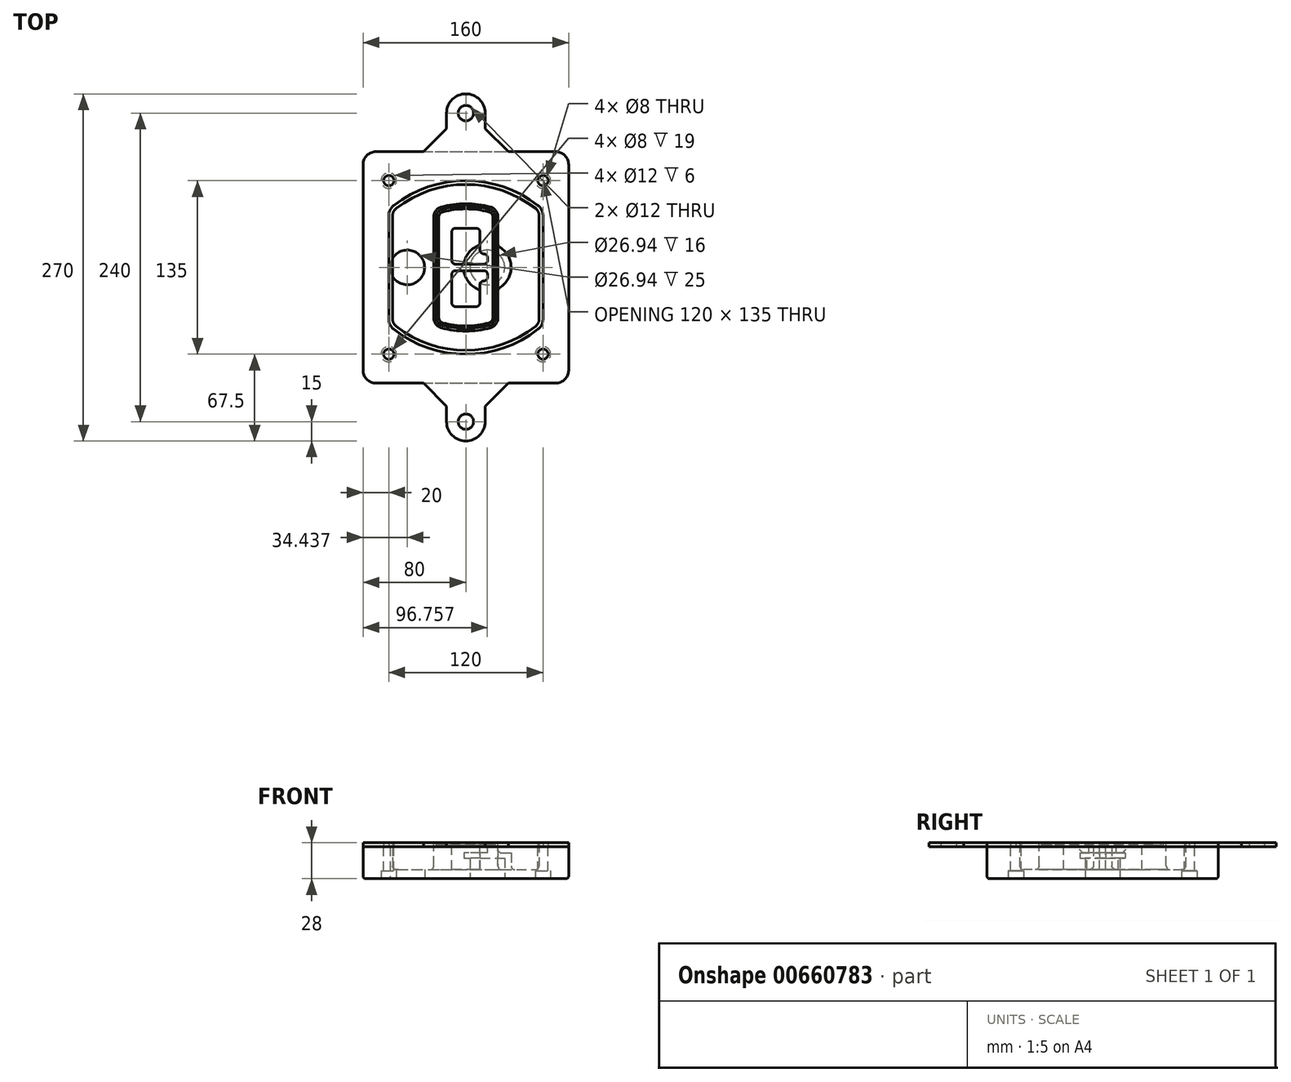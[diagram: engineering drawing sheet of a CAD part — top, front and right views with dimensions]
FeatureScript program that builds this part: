
annotation { "Feature Type Name" : "Feature", "Feature Type Description" : "" }
export const myFeature = defineFeature(function(context is Context, id is Id, definition is map)
    precondition{}
    {
        {
            var Q0;
            Q0=qCreatedBy(makeId("Top.planeOp"),FACE);
            var sketch = newSketch(context, id + "F0", { "sketchPlane" : qUnion([Q0])});
            skPoint(sketch, "E0.rect.middle", {"position": v(0, 0) * mm});
            skLineSegment(sketch, "E1.bottom", {"start": v(-70, -90) * mm, "end": v(70, -90) * mm});
            skLineSegment(sketch, "E1.top", {"start": v(-70, 90) * mm, "end": v(70, 90) * mm});
            skLineSegment(sketch, "E1.left", {"start": v(-80, -80) * mm, "end": v(-80, 80) * mm});
            skLineSegment(sketch, "E1.right", {"start": v(80, -80) * mm, "end": v(80, 80) * mm});
            skLineSegment(sketch, "E2", {"start": v(-80, 90) * mm, "end": v(80, -90) * mm, "construction": true});
            skLineSegment(sketch, "E3", {"start": v(80, 90) * mm, "end": v(-80, -90) * mm, "construction": true});
            skCircle(sketch, "E4", {"center": v(-60, 67.5) * mm, "radius": 4 * mm});
            skCircle(sketch, "E5", {"center": v(60, 67.5) * mm, "radius": 4 * mm});
            skCircle(sketch, "E6", {"center": v(60, -67.5) * mm, "radius": 4 * mm});
            skCircle(sketch, "E7", {"center": v(-60, -67.5) * mm, "radius": 4 * mm});
            skLineSegment(sketch, "E8", {"start": v(-60, 67.5) * mm, "end": v(60, 67.5) * mm, "construction": true});
            skLineSegment(sketch, "E9", {"start": v(60, 67.5) * mm, "end": v(60, -67.5) * mm, "construction": true});
            skLineSegment(sketch, "E10", {"start": v(60, -67.5) * mm, "end": v(-60, -67.5) * mm, "construction": true});
            skLineSegment(sketch, "E11", {"start": v(-60, -67.5) * mm, "end": v(-60, 67.5) * mm, "construction": true});
            skLineSegment(sketch, "E12", {"start": v(-60, 40.3) * mm, "end": v(-60, -40.3) * mm});
            skLineSegment(sketch, "E13", {"start": v(60, 40.3) * mm, "end": v(60, -40.3) * mm});
            skArc(sketch, "E14", {"start": v(56.15, 48.18) * mm, "mid": v(0, 67.5) * mm, "end": v(-56.15, 48.18) * mm});
            skArc(sketch, "E15", {"start": v(-56.15, -48.18) * mm, "mid": v(0, -67.5) * mm, "end": v(56.15, -48.18) * mm});
            skLineSegment(sketch, "E16", {"start": v(-60, 0) * mm, "end": v(60, 0) * mm, "construction": true});
            skPoint(sketch, "E17.visualSharp", {"position": v(-60, -45) * mm});
            skArc(sketch, "E17.filletArc", {"start": v(-60, -40.3) * mm, "mid": v(-58.99, -44.68) * mm, "end": v(-56.15, -48.18) * mm});
            skPoint(sketch, "E18.visualSharp", {"position": v(-60, 45) * mm});
            skArc(sketch, "E18.filletArc", {"start": v(-56.15, 48.18) * mm, "mid": v(-58.99, 44.68) * mm, "end": v(-60, 40.3) * mm});
            skPoint(sketch, "E19.visualSharp", {"position": v(60, 45) * mm});
            skArc(sketch, "E19.filletArc", {"start": v(60, 40.3) * mm, "mid": v(58.99, 44.68) * mm, "end": v(56.15, 48.18) * mm});
            skPoint(sketch, "E20.visualSharp", {"position": v(60, -45) * mm});
            skArc(sketch, "E20.filletArc", {"start": v(56.15, -48.18) * mm, "mid": v(58.99, -44.68) * mm, "end": v(60, -40.3) * mm});
            skPoint(sketch, "E21.visualSharp", {"position": v(-80, 90) * mm});
            skArc(sketch, "E21.filletArc", {"start": v(-70, 90) * mm, "mid": v(-77.07, 87.07) * mm, "end": v(-80, 80) * mm});
            skPoint(sketch, "E22.visualSharp", {"position": v(80, 90) * mm});
            skArc(sketch, "E22.filletArc", {"start": v(80, 80) * mm, "mid": v(77.07, 87.07) * mm, "end": v(70, 90) * mm});
            skPoint(sketch, "E23.visualSharp", {"position": v(80, -90) * mm});
            skArc(sketch, "E23.filletArc", {"start": v(70, -90) * mm, "mid": v(77.07, -87.07) * mm, "end": v(80, -80) * mm});
            skPoint(sketch, "E24.visualSharp", {"position": v(-80, -90) * mm});
            skArc(sketch, "E24.filletArc", {"start": v(-80, -80) * mm, "mid": v(-77.07, -87.07) * mm, "end": v(-70, -90) * mm});
            skArc(sketch, "E25.0", {"start": v(57, 40.3) * mm, "mid": v(56.3, 43.36) * mm, "end": v(54.3, 45.81) * mm});
            skLineSegment(sketch, "E25.1", {"start": v(57, 40.3) * mm, "end": v(57, -40.3) * mm});
            skArc(sketch, "E25.2", {"start": v(54.3, -45.81) * mm, "mid": v(56.3, -43.36) * mm, "end": v(57, -40.3) * mm});
            skArc(sketch, "E25.3", {"start": v(-54.3, -45.81) * mm, "mid": v(0, -64.5) * mm, "end": v(54.3, -45.81) * mm});
            skArc(sketch, "E25.4", {"start": v(-57, -40.3) * mm, "mid": v(-56.3, -43.36) * mm, "end": v(-54.3, -45.81) * mm});
            skArc(sketch, "E25.5", {"start": v(54.3, 45.81) * mm, "mid": v(0, 64.5) * mm, "end": v(-54.3, 45.81) * mm});
            skLineSegment(sketch, "E25.6", {"start": v(-57, 40.3) * mm, "end": v(-57, -40.3) * mm});
            skArc(sketch, "E25.7", {"start": v(-54.3, 45.81) * mm, "mid": v(-56.3, 43.36) * mm, "end": v(-57, 40.3) * mm});
            skArc(sketch, "E26.0", {"start": v(-58.62, 51.33) * mm, "mid": v(-62.58, 46.43) * mm, "end": v(-64, 40.3) * mm});
            skArc(sketch, "E26.1", {"start": v(58.62, 51.33) * mm, "mid": v(0, 71.5) * mm, "end": v(-58.62, 51.33) * mm});
            skArc(sketch, "E26.2", {"start": v(64, 40.3) * mm, "mid": v(62.58, 46.43) * mm, "end": v(58.62, 51.33) * mm});
            skLineSegment(sketch, "E26.3", {"start": v(64, 40.3) * mm, "end": v(64, -40.3) * mm});
            skArc(sketch, "E26.4", {"start": v(58.62, -51.33) * mm, "mid": v(62.58, -46.43) * mm, "end": v(64, -40.3) * mm});
            skLineSegment(sketch, "E26.5", {"start": v(-64, 40.3) * mm, "end": v(-64, -40.3) * mm});
            skArc(sketch, "E26.6", {"start": v(-58.62, -51.33) * mm, "mid": v(0, -71.5) * mm, "end": v(58.62, -51.33) * mm});
            skArc(sketch, "E26.7", {"start": v(-64, -40.3) * mm, "mid": v(-62.58, -46.43) * mm, "end": v(-58.62, -51.33) * mm});
            skSolve(sketch);
        }
        {
            var Q0;
            Q0=makeQuery(id+"F0.imprint","IMPRINT",FACE,{"disambiguationData":[TD([[makeQuery(id+"F0.imprint","IMPRINT",EDGE,{"derivedFrom":sQuery(id+"F0.wireOp",EDGE,"E1.bottom")}),1.0]])]});
            var Q1;
            Q1=makeQuery(id+"F0.imprint","IMPRINT",FACE,{"disambiguationData":[TD([[makeQuery(id+"F0.imprint","IMPRINT",EDGE,{"derivedFrom":sQuery(id+"F0.wireOp",EDGE,"E12")}),1.0]])]});
            var Q2;
            Q2=makeQuery(id+"F0.imprint","IMPRINT",FACE,{"disambiguationData":[TD([[makeQuery(id+"F0.imprint","IMPRINT",EDGE,{"derivedFrom":sQuery(id+"F0.wireOp",EDGE,"E25.0")}),1.0]])]});
            var Q3;
            Q3=makeQuery(id+"F0.imprint","IMPRINT",FACE,{"disambiguationData":[TD([[makeQuery(id+"F0.imprint","IMPRINT",EDGE,{"derivedFrom":sQuery(id+"F0.wireOp",EDGE,"E12")}),-1.0]])]});
            extrude(context, id + "F1", {"entities" : qUnion([Q0, Q1, Q2, Q3]), "oppositeDirection" : true, "depth" : 25 * mm});
        }
        {
            var Q0;
            Q0=makeQuery(id+"F0.imprint","IMPRINT",FACE,{"disambiguationData":[TD([[makeQuery(id+"F0.imprint","IMPRINT",EDGE,{"derivedFrom":sQuery(id+"F0.wireOp",EDGE,"E12")}),1.0]])]});
            extrude(context, id + "F2", {"entities" : qUnion([Q0]), "operationType" : NewBodyOperationType.ADD, "depth" : 3 * mm});
        }
        {
            var Q0;
            Q0=makeQuery(id+"F0.imprint","IMPRINT",FACE,{"disambiguationData":[TD([[makeQuery(id+"F0.imprint","IMPRINT",EDGE,{"derivedFrom":sQuery(id+"F0.wireOp",EDGE,"E25.0")}),1.0]])]});
            extrude(context, id + "F3", {"entities" : qUnion([Q0]), "operationType" : NewBodyOperationType.REMOVE, "oppositeDirection" : true, "depth" : 18 * mm});
        }
        {
            var Q0;
            Q0=makeQuery(id+"F2.opExtrude","CAP_FACE",FACE,{"disambiguationData":[OSD([sQuery(id+"F0.wireOp",EDGE,"E12"),sQuery(id+"F0.wireOp",EDGE,"E13"),sQuery(id+"F0.wireOp",EDGE,"E14"),sQuery(id+"F0.wireOp",EDGE,"E15"),sQuery(id+"F0.wireOp",EDGE,"E17.filletArc"),sQuery(id+"F0.wireOp",EDGE,"E18.filletArc"),sQuery(id+"F0.wireOp",EDGE,"E19.filletArc"),sQuery(id+"F0.wireOp",EDGE,"E20.filletArc"),sQuery(id+"F0.wireOp",EDGE,"E25.0"),sQuery(id+"F0.wireOp",EDGE,"E25.1"),sQuery(id+"F0.wireOp",EDGE,"E25.2"),sQuery(id+"F0.wireOp",EDGE,"E25.3"),sQuery(id+"F0.wireOp",EDGE,"E25.4"),sQuery(id+"F0.wireOp",EDGE,"E25.5"),sQuery(id+"F0.wireOp",EDGE,"E25.6"),sQuery(id+"F0.wireOp",EDGE,"E25.7")])],"isStart":false});
            var sketch = newSketch(context, id + "F4", { "sketchPlane" : qUnion([Q0])});
            skArc(sketch, "E27.0", {"start": v(-19.08, -46.97) * mm, "mid": v(0, -49.5) * mm, "end": v(19.08, -46.97) * mm});
            skArc(sketch, "E28.0", {"start": v(19.08, 46.97) * mm, "mid": v(0, 49.5) * mm, "end": v(-19.08, 46.97) * mm});
            skLineSegment(sketch, "E29", {"start": v(-25, 39.25) * mm, "end": v(-25, -39.25) * mm});
            skLineSegment(sketch, "E30", {"start": v(25, 39.25) * mm, "end": v(25, -39.25) * mm});
            skLineSegment(sketch, "E31", {"start": v(-25, 45.1) * mm, "end": v(25, 45.1) * mm, "construction": true});
            skLineSegment(sketch, "E32", {"start": v(-25, -45.1) * mm, "end": v(25, -45.1) * mm, "construction": true});
            skPoint(sketch, "E33.visualSharp", {"position": v(-25, 45.1) * mm});
            skArc(sketch, "E33.filletArc", {"start": v(-19.08, 46.97) * mm, "mid": v(-23.35, 44.11) * mm, "end": v(-25, 39.25) * mm});
            skPoint(sketch, "E34.visualSharp", {"position": v(25, 45.1) * mm});
            skArc(sketch, "E34.filletArc", {"start": v(25, 39.25) * mm, "mid": v(23.35, 44.11) * mm, "end": v(19.08, 46.97) * mm});
            skPoint(sketch, "E35.visualSharp", {"position": v(25, -45.1) * mm});
            skArc(sketch, "E35.filletArc", {"start": v(19.08, -46.97) * mm, "mid": v(23.35, -44.11) * mm, "end": v(25, -39.25) * mm});
            skPoint(sketch, "E36.visualSharp", {"position": v(-25, -45.1) * mm});
            skArc(sketch, "E36.filletArc", {"start": v(-25, -39.25) * mm, "mid": v(-23.35, -44.11) * mm, "end": v(-19.08, -46.97) * mm});
            skArc(sketch, "E37.0", {"start": v(54.3, 45.81) * mm, "mid": v(0, 64.5) * mm, "end": v(-54.3, 45.81) * mm});
            skArc(sketch, "E37.1", {"start": v(-54.3, 45.81) * mm, "mid": v(-56.3, 43.36) * mm, "end": v(-57, 40.3) * mm});
            skLineSegment(sketch, "E37.2", {"start": v(-57, 40.3) * mm, "end": v(-57, -40.3) * mm});
            skArc(sketch, "E37.3", {"start": v(-57, -40.3) * mm, "mid": v(-56.3, -43.36) * mm, "end": v(-54.3, -45.81) * mm});
            skArc(sketch, "E37.4", {"start": v(-54.3, -45.81) * mm, "mid": v(0, -64.5) * mm, "end": v(54.3, -45.81) * mm});
            skArc(sketch, "E37.5", {"start": v(54.3, -45.81) * mm, "mid": v(56.3, -43.36) * mm, "end": v(57, -40.3) * mm});
            skLineSegment(sketch, "E37.6", {"start": v(57, 40.3) * mm, "end": v(57, -40.3) * mm});
            skArc(sketch, "E37.7", {"start": v(57, 40.3) * mm, "mid": v(56.3, 43.36) * mm, "end": v(54.3, 45.81) * mm});
            skLineSegment(sketch, "E38.0", {"start": v(23, 39.25) * mm, "end": v(23, -39.25) * mm});
            skArc(sketch, "E38.1", {"start": v(18.56, -45.04) * mm, "mid": v(21.76, -42.9) * mm, "end": v(23, -39.25) * mm});
            skArc(sketch, "E38.2", {"start": v(-18.56, -45.04) * mm, "mid": v(0, -47.5) * mm, "end": v(18.56, -45.04) * mm});
            skArc(sketch, "E38.3", {"start": v(-23, -39.25) * mm, "mid": v(-21.76, -42.9) * mm, "end": v(-18.56, -45.04) * mm});
            skLineSegment(sketch, "E38.4", {"start": v(-23, 39.25) * mm, "end": v(-23, -39.25) * mm});
            skArc(sketch, "E38.5", {"start": v(23, 39.25) * mm, "mid": v(21.76, 42.9) * mm, "end": v(18.56, 45.04) * mm});
            skArc(sketch, "E38.6", {"start": v(-18.56, 45.04) * mm, "mid": v(-21.76, 42.9) * mm, "end": v(-23, 39.25) * mm});
            skArc(sketch, "E38.7", {"start": v(18.56, 45.04) * mm, "mid": v(0, 47.5) * mm, "end": v(-18.56, 45.04) * mm});
            skArc(sketch, "E39.0", {"start": v(21, 39.25) * mm, "mid": v(20.18, 41.68) * mm, "end": v(18.04, 43.1) * mm});
            skLineSegment(sketch, "E39.1", {"start": v(21, 39.25) * mm, "end": v(21, -39.25) * mm});
            skArc(sketch, "E39.2", {"start": v(18.04, -43.1) * mm, "mid": v(20.18, -41.68) * mm, "end": v(21, -39.25) * mm});
            skArc(sketch, "E39.3", {"start": v(-18.04, -43.1) * mm, "mid": v(0, -45.5) * mm, "end": v(18.04, -43.1) * mm});
            skArc(sketch, "E39.4", {"start": v(-21, -39.25) * mm, "mid": v(-20.18, -41.68) * mm, "end": v(-18.04, -43.1) * mm});
            skArc(sketch, "E39.5", {"start": v(18.04, 43.1) * mm, "mid": v(0, 45.5) * mm, "end": v(-18.04, 43.1) * mm});
            skLineSegment(sketch, "E39.6", {"start": v(-21, 39.25) * mm, "end": v(-21, -39.25) * mm});
            skArc(sketch, "E39.7", {"start": v(-18.04, 43.1) * mm, "mid": v(-20.18, 41.68) * mm, "end": v(-21, 39.25) * mm});
            skLineSegment(sketch, "E40", {"start": v(-25, 0) * mm, "end": v(25, 0) * mm, "construction": true});
            skLineSegment(sketch, "E41", {"start": v(-11, 5.5) * mm, "end": v(-11, 27.5) * mm});
            skLineSegment(sketch, "E42", {"start": v(-8, 30.5) * mm, "end": v(8, 30.5) * mm});
            skLineSegment(sketch, "E43", {"start": v(11, 27.5) * mm, "end": v(11, 13.5) * mm});
            skLineSegment(sketch, "E44", {"start": v(14, 10.5) * mm, "end": v(14, 10.5) * mm});
            skLineSegment(sketch, "E45", {"start": v(17, 7.5) * mm, "end": v(17, 5.5) * mm});
            skLineSegment(sketch, "E46", {"start": v(14, 2.5) * mm, "end": v(-8, 2.5) * mm});
            skPoint(sketch, "E47.visualSharp", {"position": v(-11, 30.5) * mm});
            skArc(sketch, "E47.filletArc", {"start": v(-8, 30.5) * mm, "mid": v(-10.12, 29.62) * mm, "end": v(-11, 27.5) * mm});
            skPoint(sketch, "E48.visualSharp", {"position": v(11, 30.5) * mm});
            skArc(sketch, "E48.filletArc", {"start": v(11, 27.5) * mm, "mid": v(10.12, 29.62) * mm, "end": v(8, 30.5) * mm});
            skPoint(sketch, "E49.visualSharp", {"position": v(11, 10.5) * mm});
            skArc(sketch, "E49.filletArc", {"start": v(11, 13.5) * mm, "mid": v(11.88, 11.38) * mm, "end": v(14, 10.5) * mm});
            skPoint(sketch, "E50.visualSharp", {"position": v(17, 10.5) * mm});
            skArc(sketch, "E50.filletArc", {"start": v(17, 7.5) * mm, "mid": v(16.12, 9.62) * mm, "end": v(14, 10.5) * mm});
            skPoint(sketch, "E51.visualSharp", {"position": v(17, 2.5) * mm});
            skArc(sketch, "E51.filletArc", {"start": v(14, 2.5) * mm, "mid": v(16.12, 3.38) * mm, "end": v(17, 5.5) * mm});
            skPoint(sketch, "E52.visualSharp", {"position": v(-11, 2.5) * mm});
            skArc(sketch, "E52.filletArc", {"start": v(-11, 5.5) * mm, "mid": v(-10.12, 3.38) * mm, "end": v(-8, 2.5) * mm});
            skLineSegment(sketch, "E53.0.MirrorCS", {"start": v(14, -2.5) * mm, "end": v(-8, -2.5) * mm});
            skArc(sketch, "E54.0.MirrorCS", {"start": v(-11, -5.5) * mm, "mid": v(-10.12, -3.38) * mm, "end": v(-8, -2.5) * mm});
            skLineSegment(sketch, "E55.0.MirrorCS", {"start": v(-11, -5.5) * mm, "end": v(-11, -27.5) * mm});
            skArc(sketch, "E56.0.MirrorCS", {"start": v(-8, -30.5) * mm, "mid": v(-10.12, -29.62) * mm, "end": v(-11, -27.5) * mm});
            skLineSegment(sketch, "E57.0.MirrorCS", {"start": v(-8, -30.5) * mm, "end": v(8, -30.5) * mm});
            skArc(sketch, "E58.0.MirrorCS", {"start": v(11, -27.5) * mm, "mid": v(10.12, -29.62) * mm, "end": v(8, -30.5) * mm});
            skLineSegment(sketch, "E59.0.MirrorCS", {"start": v(11, -27.5) * mm, "end": v(11, -13.5) * mm});
            skArc(sketch, "E60.0.MirrorCS", {"start": v(11, -13.5) * mm, "mid": v(11.88, -11.38) * mm, "end": v(14, -10.5) * mm});
            skArc(sketch, "E61.0.MirrorCS", {"start": v(17, -7.5) * mm, "mid": v(16.12, -9.62) * mm, "end": v(14, -10.5) * mm});
            skLineSegment(sketch, "E62.0.MirrorCS", {"start": v(17, -7.5) * mm, "end": v(17, -5.5) * mm});
            skArc(sketch, "E63.0.MirrorCS", {"start": v(14, -2.5) * mm, "mid": v(16.12, -3.38) * mm, "end": v(17, -5.5) * mm});
            skSolve(sketch);
        }
        {
            var Q0;
            Q0=makeQuery(id+"F4.imprint","IMPRINT",FACE,{"disambiguationData":[TD([[makeQuery(id+"F4.imprint","IMPRINT",EDGE,{"derivedFrom":sQuery(id+"F4.wireOp",EDGE,"E27.0")}),1.0]])]});
            var Q1;
            Q1=makeQuery(id+"F4.imprint","IMPRINT",FACE,{"disambiguationData":[TD([[makeQuery(id+"F4.imprint","IMPRINT",EDGE,{"derivedFrom":sQuery(id+"F4.wireOp",EDGE,"E38.0")}),-1.0]])]});
            var Q2;
            Q2=makeQuery(id+"F4.imprint","IMPRINT",FACE,{"disambiguationData":[TD([[makeQuery(id+"F4.imprint","IMPRINT",EDGE,{"derivedFrom":sQuery(id+"F4.wireOp",EDGE,"E39.0")}),1.0]])]});
            extrude(context, id + "F5", {"entities" : qUnion([Q0, Q1, Q2]), "operationType" : NewBodyOperationType.ADD, "endBound" : BoundingType.UP_TO_NEXT, "oppositeDirection" : true, "depth" : 25 * mm});
        }
        {
            var Q0;
            Q0=makeQuery(id+"F4.imprint","IMPRINT",FACE,{"disambiguationData":[TD([[makeQuery(id+"F4.imprint","IMPRINT",EDGE,{"derivedFrom":sQuery(id+"F4.wireOp",EDGE,"E38.0")}),-1.0]])]});
            extrude(context, id + "F6", {"entities" : qUnion([Q0]), "operationType" : NewBodyOperationType.REMOVE, "oppositeDirection" : true, "depth" : 2 * mm});
        }
        {
            var Q0;
            Q0=makeQuery(id+"F1.opExtrude","CAP_FACE",FACE,{"disambiguationData":[OSD([sQuery(id+"F0.wireOp",EDGE,"E1.bottom"),sQuery(id+"F0.wireOp",EDGE,"E1.top"),sQuery(id+"F0.wireOp",EDGE,"E1.left"),sQuery(id+"F0.wireOp",EDGE,"E1.right"),sQuery(id+"F0.wireOp",EDGE,"E4"),sQuery(id+"F0.wireOp",EDGE,"E5"),sQuery(id+"F0.wireOp",EDGE,"E6"),sQuery(id+"F0.wireOp",EDGE,"E7"),sQuery(id+"F0.wireOp",EDGE,"E21.filletArc"),sQuery(id+"F0.wireOp",EDGE,"E22.filletArc"),sQuery(id+"F0.wireOp",EDGE,"E23.filletArc"),sQuery(id+"F0.wireOp",EDGE,"E24.filletArc")])],"isStart":false});
            var sketch = newSketch(context, id + "F7", { "sketchPlane" : qUnion([Q0])});
            skCircle(sketch, "E64", {"center": v(16.76, 0) * mm, "radius": 13.47 * mm});
            skCircle(sketch, "E65", {"center": v(-45.56, 0) * mm, "radius": 13.47 * mm});
            skLineSegment(sketch, "E66", {"start": v(80, 0) * mm, "end": v(-80, 0) * mm});
            skCircle(sketch, "E67", {"center": v(16.76, 0) * mm, "radius": 18.47 * mm});
            skCircle(sketch, "E68", {"center": v(60, -67.5) * mm, "radius": 6 * mm});
            skCircle(sketch, "E69", {"center": v(-60, -67.5) * mm, "radius": 6 * mm});
            skCircle(sketch, "E70", {"center": v(-60, 67.5) * mm, "radius": 6 * mm});
            skCircle(sketch, "E71", {"center": v(60, 67.5) * mm, "radius": 6 * mm});
            skSolve(sketch);
        }
        {
            var Q0;
            {var subQ1=sQuery(id+"F7.wireOp",EDGE,"E66");var subQ4=sQuery(id+"F7.wireOp",EDGE,"E64");var subQ6=makeQuery(id+"F7.imprint","INTERSECT",VERTEX,{"disambiguationData":[OD(0.0)],"derivedFrom":[subQ4,subQ1]});Q0=makeQuery(id+"F7.imprint","IMPRINT",FACE,{"disambiguationData":[TD([[makeQuery(id+"F7.imprint","IMPRINT",EDGE,{"disambiguationData":[TD([[subQ6,-1.0]])],"derivedFrom":subQ4}),-1.0]])]});}
            var Q1;
            {var subQ0=sQuery(id+"F7.wireOp",EDGE,"E66");var subQ1=sQuery(id+"F7.wireOp",EDGE,"E64");var subQ3=makeQuery(id+"F7.imprint","INTERSECT",VERTEX,{"disambiguationData":[OD(0.0)],"derivedFrom":[subQ1,subQ0]});Q1=makeQuery(id+"F7.imprint","IMPRINT",FACE,{"disambiguationData":[TD([[makeQuery(id+"F7.imprint","IMPRINT",EDGE,{"disambiguationData":[TD([[subQ3,-1.0]])],"derivedFrom":subQ1}),1.0]])]});}
            var Q2;
            {var subQ0=sQuery(id+"F7.wireOp",EDGE,"E66");var subQ1=sQuery(id+"F7.wireOp",EDGE,"E64");var subQ3=makeQuery(id+"F7.imprint","INTERSECT",VERTEX,{"disambiguationData":[OD(0.0)],"derivedFrom":[subQ1,subQ0]});Q2=makeQuery(id+"F7.imprint","IMPRINT",FACE,{"disambiguationData":[TD([[makeQuery(id+"F7.imprint","IMPRINT",EDGE,{"disambiguationData":[TD([[subQ3,1.0]])],"derivedFrom":subQ1}),1.0]])]});}
            var Q3;
            {var subQ1=sQuery(id+"F7.wireOp",EDGE,"E66");var subQ4=sQuery(id+"F7.wireOp",EDGE,"E64");var subQ6=makeQuery(id+"F7.imprint","INTERSECT",VERTEX,{"disambiguationData":[OD(0.0)],"derivedFrom":[subQ4,subQ1]});Q3=makeQuery(id+"F7.imprint","IMPRINT",FACE,{"disambiguationData":[TD([[makeQuery(id+"F7.imprint","IMPRINT",EDGE,{"disambiguationData":[TD([[subQ6,1.0]])],"derivedFrom":subQ4}),-1.0]])]});}
            extrude(context, id + "F8", {"entities" : qUnion([Q0, Q1, Q2, Q3]), "operationType" : NewBodyOperationType.ADD, "oppositeDirection" : true, "depth" : 20 * mm});
        }
        {
            var Q0;
            {var subQ0=sQuery(id+"F7.wireOp",EDGE,"E66");var subQ1=sQuery(id+"F7.wireOp",EDGE,"E64");var subQ3=makeQuery(id+"F7.imprint","INTERSECT",VERTEX,{"disambiguationData":[OD(0.0)],"derivedFrom":[subQ1,subQ0]});Q0=makeQuery(id+"F7.imprint","IMPRINT",FACE,{"disambiguationData":[TD([[makeQuery(id+"F7.imprint","IMPRINT",EDGE,{"disambiguationData":[TD([[subQ3,-1.0]])],"derivedFrom":subQ1}),1.0]])]});}
            var Q1;
            {var subQ0=sQuery(id+"F7.wireOp",EDGE,"E66");var subQ1=sQuery(id+"F7.wireOp",EDGE,"E64");var subQ3=makeQuery(id+"F7.imprint","INTERSECT",VERTEX,{"disambiguationData":[OD(0.0)],"derivedFrom":[subQ1,subQ0]});Q1=makeQuery(id+"F7.imprint","IMPRINT",FACE,{"disambiguationData":[TD([[makeQuery(id+"F7.imprint","IMPRINT",EDGE,{"disambiguationData":[TD([[subQ3,1.0]])],"derivedFrom":subQ1}),1.0]])]});}
            extrude(context, id + "F9", {"entities" : qUnion([Q0, Q1]), "operationType" : NewBodyOperationType.REMOVE, "oppositeDirection" : true, "depth" : 16 * mm});
        }
        {
            var Q0;
            {var subQ0=sQuery(id+"F7.wireOp",EDGE,"E66");var subQ1=sQuery(id+"F7.wireOp",EDGE,"E65");var subQ3=makeQuery(id+"F7.imprint","INTERSECT",VERTEX,{"disambiguationData":[OD(0.0)],"derivedFrom":[subQ1,subQ0]});Q0=makeQuery(id+"F7.imprint","IMPRINT",FACE,{"disambiguationData":[TD([[makeQuery(id+"F7.imprint","IMPRINT",EDGE,{"disambiguationData":[TD([[subQ3,-1.0]])],"derivedFrom":subQ1}),1.0]])]});}
            var Q1;
            {var subQ0=sQuery(id+"F7.wireOp",EDGE,"E66");var subQ1=sQuery(id+"F7.wireOp",EDGE,"E65");var subQ3=makeQuery(id+"F7.imprint","INTERSECT",VERTEX,{"disambiguationData":[OD(0.0)],"derivedFrom":[subQ1,subQ0]});Q1=makeQuery(id+"F7.imprint","IMPRINT",FACE,{"disambiguationData":[TD([[makeQuery(id+"F7.imprint","IMPRINT",EDGE,{"disambiguationData":[TD([[subQ3,1.0]])],"derivedFrom":subQ1}),1.0]])]});}
            extrude(context, id + "F10", {"entities" : qUnion([Q0, Q1]), "operationType" : NewBodyOperationType.REMOVE, "oppositeDirection" : true, "depth" : 25 * mm});
        }
        {
            var Q0;
            Q0=makeQuery(id+"F7.imprint","IMPRINT",FACE,{"disambiguationData":[TD([[makeQuery(id+"F7.imprint","IMPRINT",EDGE,{"derivedFrom":sQuery(id+"F7.wireOp",EDGE,"E68")}),1.0]])]});
            var Q1;
            Q1=makeQuery(id+"F7.imprint","IMPRINT",FACE,{"disambiguationData":[TD([[makeQuery(id+"F7.imprint","IMPRINT",EDGE,{"derivedFrom":makeQuery(id+"F1.opExtrude","CAP_EDGE",EDGE,{"disambiguationData":[OSD([sQuery(id+"F0.wireOp",EDGE,"E5")])],"isStart":false})}),-1.0]])]});
            var Q2;
            Q2=makeQuery(id+"F7.imprint","IMPRINT",FACE,{"disambiguationData":[TD([[makeQuery(id+"F7.imprint","IMPRINT",EDGE,{"derivedFrom":sQuery(id+"F7.wireOp",EDGE,"E69")}),1.0]])]});
            var Q3;
            Q3=makeQuery(id+"F7.imprint","IMPRINT",FACE,{"disambiguationData":[TD([[makeQuery(id+"F7.imprint","IMPRINT",EDGE,{"derivedFrom":makeQuery(id+"F1.opExtrude","CAP_EDGE",EDGE,{"disambiguationData":[OSD([sQuery(id+"F0.wireOp",EDGE,"E4")])],"isStart":false})}),-1.0]])]});
            var Q4;
            Q4=makeQuery(id+"F7.imprint","IMPRINT",FACE,{"disambiguationData":[TD([[makeQuery(id+"F7.imprint","IMPRINT",EDGE,{"derivedFrom":sQuery(id+"F7.wireOp",EDGE,"E70")}),1.0]])]});
            var Q5;
            Q5=makeQuery(id+"F7.imprint","IMPRINT",FACE,{"disambiguationData":[TD([[makeQuery(id+"F7.imprint","IMPRINT",EDGE,{"derivedFrom":makeQuery(id+"F1.opExtrude","CAP_EDGE",EDGE,{"disambiguationData":[OSD([sQuery(id+"F0.wireOp",EDGE,"E7")])],"isStart":false})}),-1.0]])]});
            var Q6;
            Q6=makeQuery(id+"F7.imprint","IMPRINT",FACE,{"disambiguationData":[TD([[makeQuery(id+"F7.imprint","IMPRINT",EDGE,{"derivedFrom":sQuery(id+"F7.wireOp",EDGE,"E71")}),1.0]])]});
            var Q7;
            Q7=makeQuery(id+"F7.imprint","IMPRINT",FACE,{"disambiguationData":[TD([[makeQuery(id+"F7.imprint","IMPRINT",EDGE,{"derivedFrom":makeQuery(id+"F1.opExtrude","CAP_EDGE",EDGE,{"disambiguationData":[OSD([sQuery(id+"F0.wireOp",EDGE,"E6")])],"isStart":false})}),-1.0]])]});
            extrude(context, id + "F11", {"entities" : qUnion([Q0, Q1, Q2, Q3, Q4, Q5, Q6, Q7]), "operationType" : NewBodyOperationType.REMOVE, "oppositeDirection" : true, "depth" : 6 * mm});
        }
        {
            var Q0;
            Q0=makeQuery(id+"F9.boolean.opBoolean","COPY",FACE,{"derivedFrom":makeQuery(id+"F9.opExtrude","CAP_FACE",FACE,{"disambiguationData":[OSD([sQuery(id+"F7.wireOp",EDGE,"E64")])],"isStart":false})});
            var sketch = newSketch(context, id + "F12", { "sketchPlane" : qUnion([Q0])});
            skArc(sketch, "E72.0", {"start": v(11, 17.55) * mm, "mid": v(2.57, 11.82) * mm, "end": v(-1.54, 2.5) * mm});
            skArc(sketch, "E72.1", {"start": v(-1.54, -2.5) * mm, "mid": v(2.57, -11.82) * mm, "end": v(11, -17.55) * mm});
            skLineSegment(sketch, "E73", {"start": v(-1.54, -2.5) * mm, "end": v(14, -2.5) * mm});
            skLineSegment(sketch, "E74.0", {"start": v(14, 2.5) * mm, "end": v(-1.54, 2.5) * mm});
            skArc(sketch, "E74.1", {"start": v(14, 2.5) * mm, "mid": v(16.12, 3.38) * mm, "end": v(17, 5.5) * mm});
            skLineSegment(sketch, "E74.2", {"start": v(17, 7.5) * mm, "end": v(17, 5.5) * mm});
            skArc(sketch, "E74.3", {"start": v(17, 7.5) * mm, "mid": v(16.12, 9.62) * mm, "end": v(14, 10.5) * mm});
            skArc(sketch, "E74.4", {"start": v(11, 13.5) * mm, "mid": v(11.88, 11.38) * mm, "end": v(14, 10.5) * mm});
            skLineSegment(sketch, "E74.5", {"start": v(11, 17.55) * mm, "end": v(11, 13.5) * mm});
            skLineSegment(sketch, "E74.7", {"start": v(14, -2.5) * mm, "end": v(-1.54, -2.5) * mm});
            skArc(sketch, "E74.8", {"start": v(14, -2.5) * mm, "mid": v(16.12, -3.38) * mm, "end": v(17, -5.5) * mm});
            skLineSegment(sketch, "E74.9", {"start": v(17, -7.5) * mm, "end": v(17, -5.5) * mm});
            skArc(sketch, "E74.10", {"start": v(17, -7.5) * mm, "mid": v(16.12, -9.62) * mm, "end": v(14, -10.5) * mm});
            skArc(sketch, "E74.11", {"start": v(11, -13.5) * mm, "mid": v(11.88, -11.38) * mm, "end": v(14, -10.5) * mm});
            skLineSegment(sketch, "E74.12", {"start": v(11, -17.55) * mm, "end": v(11, -13.5) * mm});
            skPoint(sketch, "E75.orphan", {"position": v(11, -27.5) * mm});
            skPoint(sketch, "E76.orphan", {"position": v(-8, -2.5) * mm});
            skPoint(sketch, "E77.orphan", {"position": v(-8, 2.5) * mm});
            skPoint(sketch, "E78.orphan", {"position": v(11, 27.5) * mm});
            skSolve(sketch);
        }
        {
            var Q0;
            {var subQ7=sQuery(id+"F12.wireOp",EDGE,"E72.0");var subQ14=sQuery(id+"F12.wireOp",EDGE,"E72.1");var subQ16=sQuery(id+"F12.wireOp",EDGE,"E74.1");var subQ18=sQuery(id+"F12.wireOp",EDGE,"E74.8");Q0=qUnion([makeQuery(id+"F12.imprint","IMPRINT",FACE,{"disambiguationData":[TD([[makeQuery(id+"F12.imprint","IMPRINT",EDGE,{"derivedFrom":subQ7}),1.0]])]}),makeQuery(id+"F12.imprint","IMPRINT",FACE,{"disambiguationData":[TD([[makeQuery(id+"F12.imprint","IMPRINT",EDGE,{"derivedFrom":subQ14}),1.0]])]}),makeQuery(id+"F12.imprint","IMPRINT",FACE,{"disambiguationData":[TD([[makeQuery(id+"F12.imprint","IMPRINT",EDGE,{"derivedFrom":subQ16}),1.0]])]}),makeQuery(id+"F12.imprint","IMPRINT",FACE,{"disambiguationData":[TD([[makeQuery(id+"F12.imprint","IMPRINT",EDGE,{"derivedFrom":subQ18}),-1.0]])]})]);}
            var Q1;
            Q1=makeQuery(id+"F5.boolean.opBoolean","SPLIT",FACE,{"disambiguationData":[TD([makeQuery(id+"F5.opExtrude","SWEPT_FACE",FACE,{"disambiguationData":[OSD([sQuery(id+"F4.wireOp",EDGE,"E41")])]})])],"derivedFrom":makeQuery(id+"F3.boolean.opBoolean","COPY",FACE,{"derivedFrom":makeQuery(id+"F3.opExtrude","CAP_FACE",FACE,{"disambiguationData":[OSD([sQuery(id+"F0.wireOp",EDGE,"E25.0"),sQuery(id+"F0.wireOp",EDGE,"E25.1"),sQuery(id+"F0.wireOp",EDGE,"E25.2"),sQuery(id+"F0.wireOp",EDGE,"E25.3"),sQuery(id+"F0.wireOp",EDGE,"E25.4"),sQuery(id+"F0.wireOp",EDGE,"E25.5"),sQuery(id+"F0.wireOp",EDGE,"E25.6"),sQuery(id+"F0.wireOp",EDGE,"E25.7")])],"isStart":false})})});
            extrude(context, id + "F13", {"entities" : qUnion([Q0]), "operationType" : NewBodyOperationType.REMOVE, "endBound" : BoundingType.UP_TO_SURFACE, "endBoundEntityFace" : qUnion([Q1]), "depth" : 25 * mm});
        }
        {
            var Q0;
            Q0=makeQuery(id+"F3.boolean.opBoolean","COPY",EDGE,{"derivedFrom":makeQuery(id+"F3.opExtrude","CAP_EDGE",EDGE,{"disambiguationData":[OSD([sQuery(id+"F0.wireOp",EDGE,"E25.6")])],"isStart":false})});
            var Q1;
            Q1=makeQuery(id+"F8.boolean.opBoolean","INTERSECT",EDGE,{"derivedFrom":[makeQuery(id+"F5.opExtrude","SWEPT_FACE",FACE,{"disambiguationData":[OSD([sQuery(id+"F4.wireOp",EDGE,"E30")])]}),makeQuery(id+"F8.opExtrude","CAP_FACE",FACE,{"disambiguationData":[OSD([sQuery(id+"F7.wireOp",EDGE,"E67")])],"isStart":false})]});
            var Q2;
            Q2=makeQuery(id+"F8.boolean.opBoolean","INTERSECT",EDGE,{"disambiguationData":[OD(1.0)],"derivedFrom":[makeQuery(id+"F5.opExtrude","SWEPT_FACE",FACE,{"disambiguationData":[OSD([sQuery(id+"F4.wireOp",EDGE,"E30")])]}),makeQuery(id+"F8.opExtrude","SWEPT_FACE",FACE,{"disambiguationData":[OSD([sQuery(id+"F7.wireOp",EDGE,"E67")])]})]});
            var Q3;
            {var subQ0=sQuery(id+"F4.wireOp",EDGE,"E30");Q3=makeQuery(id+"F8.boolean.opBoolean","SPLIT",EDGE,{"disambiguationData":[TD([makeQuery(id+"F5.opExtrude","SWEPT_FACE",FACE,{"disambiguationData":[OSD([sQuery(id+"F4.wireOp",EDGE,"E35.filletArc")])]})])],"derivedFrom":makeQuery(id+"F5.opExtrude","CAP_EDGE",EDGE,{"disambiguationData":[OSD([subQ0])],"isStart":false})});}
            var Q4;
            {var subQ0=sQuery(id+"F0.wireOp",EDGE,"E25.7");var subQ1=sQuery(id+"F0.wireOp",EDGE,"E25.1");var subQ2=sQuery(id+"F0.wireOp",EDGE,"E25.6");var subQ3=sQuery(id+"F0.wireOp",EDGE,"E25.5");var subQ4=sQuery(id+"F0.wireOp",EDGE,"E25.4");var subQ5=sQuery(id+"F0.wireOp",EDGE,"E25.0");var subQ6=sQuery(id+"F0.wireOp",EDGE,"E25.2");var subQ7=sQuery(id+"F0.wireOp",EDGE,"E25.3");Q4=makeQuery(id+"F8.boolean.opBoolean","INTERSECT",EDGE,{"derivedFrom":[makeQuery(id+"F5.boolean.opBoolean","SPLIT",FACE,{"disambiguationData":[TD([makeQuery(id+"F2.opExtrude","SWEPT_FACE",FACE,{"disambiguationData":[OSD([subQ5])]})])],"derivedFrom":makeQuery(id+"F3.boolean.opBoolean","COPY",FACE,{"derivedFrom":makeQuery(id+"F3.opExtrude","CAP_FACE",FACE,{"disambiguationData":[OSD([subQ5,subQ1,subQ6,subQ7,subQ4,subQ3,subQ2,subQ0])],"isStart":false})})}),makeQuery(id+"F8.opExtrude","SWEPT_FACE",FACE,{"disambiguationData":[OSD([sQuery(id+"F7.wireOp",EDGE,"E67")])]})]});}
            var Q5;
            Q5=makeQuery(id+"F8.boolean.opBoolean","INTERSECT",EDGE,{"disambiguationData":[OD(0.0)],"derivedFrom":[makeQuery(id+"F5.opExtrude","SWEPT_FACE",FACE,{"disambiguationData":[OSD([sQuery(id+"F4.wireOp",EDGE,"E30")])]}),makeQuery(id+"F8.opExtrude","SWEPT_FACE",FACE,{"disambiguationData":[OSD([sQuery(id+"F7.wireOp",EDGE,"E67")])]})]});
            fillet(context, id + "F14", {"entities" : qUnion([Q0, Q1, Q2, Q3, Q4, Q5]), "radius" : 3 * mm, "tangentPropagation" : true, "allowEdgeOverflow" : false});
        }
        {
            var Q0;
            Q0=makeQuery(id+"F1.opExtrude","CAP_EDGE",EDGE,{"disambiguationData":[OSD([sQuery(id+"F0.wireOp",EDGE,"E1.bottom")])],"isStart":false});
            fillet(context, id + "F15", {"entities" : qUnion([Q0]), "radius" : 2 * mm, "tangentPropagation" : true, "allowEdgeOverflow" : false});
        }
        {
            var Q0;
            {var subQ0=sQuery(id+"F0.wireOp",EDGE,"E21.filletArc");var subQ1=sQuery(id+"F0.wireOp",EDGE,"E7");var subQ2=sQuery(id+"F0.wireOp",EDGE,"E6");var subQ3=sQuery(id+"F0.wireOp",EDGE,"E5");var subQ4=sQuery(id+"F0.wireOp",EDGE,"E4");var subQ5=sQuery(id+"F0.wireOp",EDGE,"E22.filletArc");var subQ6=sQuery(id+"F0.wireOp",EDGE,"E1.bottom");var subQ7=sQuery(id+"F0.wireOp",EDGE,"E1.right");var subQ8=sQuery(id+"F0.wireOp",EDGE,"E1.top");var subQ9=sQuery(id+"F0.wireOp",EDGE,"E1.left");var subQ10=sQuery(id+"F0.wireOp",EDGE,"E23.filletArc");var subQ11=sQuery(id+"F0.wireOp",EDGE,"E24.filletArc");Q0=makeQuery(id+"F2.boolean.opBoolean","SPLIT",FACE,{"disambiguationData":[TD([makeQuery(id+"F1.opExtrude","SWEPT_FACE",FACE,{"disambiguationData":[OSD([subQ6])]})])],"derivedFrom":makeQuery(id+"F1.opExtrude","CAP_FACE",FACE,{"disambiguationData":[OSD([subQ6,subQ8,subQ9,subQ7,subQ4,subQ3,subQ2,subQ1,subQ0,subQ5,subQ10,subQ11])],"isStart":true})});}
            var sketch = newSketch(context, id + "F16", { "sketchPlane" : qUnion([Q0])});
            skLineSegment(sketch, "E79", {"start": v(0, 90) * mm, "end": v(0, 120) * mm});
            skCircle(sketch, "E80", {"center": v(0, 120) * mm, "radius": 6 * mm});
            skArc(sketch, "E81", {"start": v(-15, 120) * mm, "mid": v(0, 135) * mm, "end": v(15, 120) * mm});
            skLineSegment(sketch, "E82", {"start": v(-15, 120) * mm, "end": v(-15, 108) * mm});
            skLineSegment(sketch, "E83", {"start": v(15, 120) * mm, "end": v(15, 108) * mm});
            skLineSegment(sketch, "E84", {"start": v(-15, 108) * mm, "end": v(-33, 90) * mm});
            skLineSegment(sketch, "E85", {"start": v(33, 90) * mm, "end": v(15, 108) * mm});
            skLineSegment(sketch, "E86", {"start": v(-80, 0) * mm, "end": v(80, 0) * mm});
            skLineSegment(sketch, "E87.MirrorCS", {"start": v(0, -90) * mm, "end": v(0, -120) * mm});
            skLineSegment(sketch, "E88.MirrorCS", {"start": v(-15, -108) * mm, "end": v(-33, -90) * mm});
            skLineSegment(sketch, "E89.MirrorCS", {"start": v(-15, -120) * mm, "end": v(-15, -108) * mm});
            skArc(sketch, "E90.MirrorCS", {"start": v(-15, -120) * mm, "mid": v(0, -135) * mm, "end": v(15, -120) * mm});
            skLineSegment(sketch, "E91.MirrorCS", {"start": v(15, -120) * mm, "end": v(15, -108) * mm});
            skLineSegment(sketch, "E92.MirrorCS", {"start": v(33, -90) * mm, "end": v(15, -108) * mm});
            skCircle(sketch, "E93.MirrorC", {"center": v(0, -120) * mm, "radius": 6 * mm});
            skText(sketch, "E94", { "text": "50865.397 mm^3\n\nMaddie Punke", "fontName": "OpenSans-Regular.ttf"});
            const initialGuessF16  = {"E94": [-0.1925, -0.19935, 1, 0, 0.05924]};
            skSetInitialGuess(sketch, initialGuessF16);
            skSolve(sketch);
        }
        {
            var Q0;
            Q0=makeQuery(id+"F16.imprint","IMPRINT",FACE,{"disambiguationData":[TD([[makeQuery(id+"F16.imprint","IMPRINT",EDGE,{"derivedFrom":makeQuery(id+"F1.opExtrude","CAP_EDGE",EDGE,{"disambiguationData":[OSD([sQuery(id+"F0.wireOp",EDGE,"E6")])],"isStart":true})}),-1.0]])]});
            var Q1;
            {var subQ3=sQuery(id+"F16.wireOp",EDGE,"E88.MirrorCS");Q1=makeQuery(id+"F16.imprint","IMPRINT",FACE,{"disambiguationData":[TD([[makeQuery(id+"F16.imprint","IMPRINT",EDGE,{"derivedFrom":subQ3}),-1.0]])]});}
            var Q2;
            Q2=makeQuery(id+"F16.imprint","IMPRINT",FACE,{"disambiguationData":[TD([[makeQuery(id+"F16.imprint","IMPRINT",EDGE,{"derivedFrom":makeQuery(id+"F1.opExtrude","CAP_EDGE",EDGE,{"disambiguationData":[OSD([sQuery(id+"F0.wireOp",EDGE,"E4")])],"isStart":true})}),-1.0]])]});
            var Q3;
            Q3=makeQuery(id+"F16.imprint","IMPRINT",FACE,{"disambiguationData":[TD([[makeQuery(id+"F16.imprint","IMPRINT",EDGE,{"derivedFrom":sQuery(id+"F16.wireOp",EDGE,"E80")}),-1.0]])]});
            var Q4;
            Q4=makeQuery(id+"F2.opExtrude","CAP_FACE",FACE,{"disambiguationData":[OSD([sQuery(id+"F0.wireOp",EDGE,"E12"),sQuery(id+"F0.wireOp",EDGE,"E13"),sQuery(id+"F0.wireOp",EDGE,"E14"),sQuery(id+"F0.wireOp",EDGE,"E15"),sQuery(id+"F0.wireOp",EDGE,"E17.filletArc"),sQuery(id+"F0.wireOp",EDGE,"E18.filletArc"),sQuery(id+"F0.wireOp",EDGE,"E19.filletArc"),sQuery(id+"F0.wireOp",EDGE,"E20.filletArc"),sQuery(id+"F0.wireOp",EDGE,"E25.0"),sQuery(id+"F0.wireOp",EDGE,"E25.1"),sQuery(id+"F0.wireOp",EDGE,"E25.2"),sQuery(id+"F0.wireOp",EDGE,"E25.3"),sQuery(id+"F0.wireOp",EDGE,"E25.4"),sQuery(id+"F0.wireOp",EDGE,"E25.5"),sQuery(id+"F0.wireOp",EDGE,"E25.6"),sQuery(id+"F0.wireOp",EDGE,"E25.7")])],"isStart":false});
            extrude(context, id + "F17", {"entities" : qUnion([Q0, Q1, Q2, Q3]), "endBound" : BoundingType.UP_TO_SURFACE, "depth" : 25 * mm, "endBoundEntityFace" : qUnion([Q4]), "offsetDistance" : 25 * mm});
        }
    });
